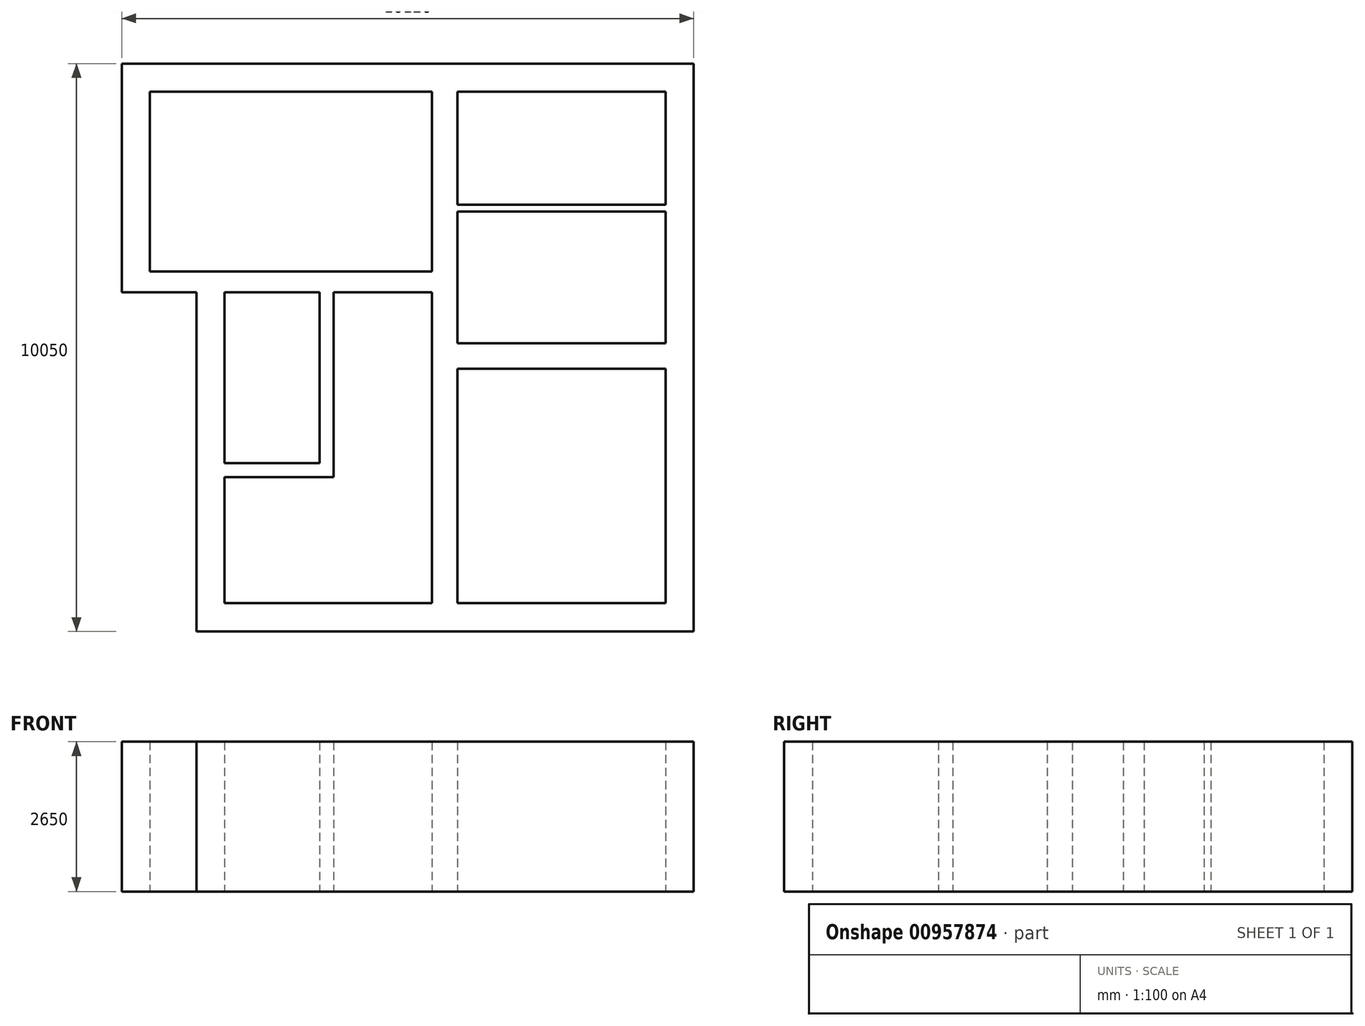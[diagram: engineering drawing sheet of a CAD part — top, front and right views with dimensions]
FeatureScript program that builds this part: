
annotation { "Feature Type Name" : "Feature", "Feature Type Description" : "" }
export const myFeature = defineFeature(function(context is Context, id is Id, definition is map)
    precondition{}
    {
        {
            var Q0;
            Q0=qCreatedBy(makeId("Top.planeOp"),FACE);
            var sketch = newSketch(context, id + "F0", { "sketchPlane" : qUnion([Q0])});
            skLineSegment(sketch, "E0", {"start": v(-6317.16, -9488.66) * mm, "end": v(2482.84, -9488.66) * mm});
            skLineSegment(sketch, "E1", {"start": v(-6317.16, -9488.66) * mm, "end": v(-6317.16, -3488.66) * mm});
            skLineSegment(sketch, "E2", {"start": v(2482.84, -9488.66) * mm, "end": v(2482.84, 561.34) * mm});
            skLineSegment(sketch, "E3", {"start": v(-5817.16, -8988.66) * mm, "end": v(-2147.16, -8988.66) * mm});
            skLineSegment(sketch, "E4", {"start": v(-5817.16, -8988.66) * mm, "end": v(-5817.16, -6758.66) * mm});
            skLineSegment(sketch, "E5", {"start": v(1982.84, 61.34) * mm, "end": v(1982.84, -1938.66) * mm});
            skLineSegment(sketch, "E6", {"start": v(1982.84, 61.34) * mm, "end": v(-1697.16, 61.34) * mm});
            skLineSegment(sketch, "E7", {"start": v(-1697.16, 61.34) * mm, "end": v(-1697.16, -1938.66) * mm});
            skLineSegment(sketch, "E8", {"start": v(-2147.16, 61.34) * mm, "end": v(-2147.16, -8988.66) * mm});
            skLineSegment(sketch, "E9", {"start": v(-2147.16, 61.34) * mm, "end": v(-7137.16, 61.34) * mm});
            skLineSegment(sketch, "E10", {"start": v(-7137.16, 61.34) * mm, "end": v(-7137.16, -3118.66) * mm});
            skLineSegment(sketch, "E11", {"start": v(2482.84, 561.34) * mm, "end": v(-7637.16, 561.34) * mm});
            skLineSegment(sketch, "E12.trimOffspring", {"start": v(-1697.16, -8988.66) * mm, "end": v(1982.84, -8988.66) * mm});
            skLineSegment(sketch, "E13", {"start": v(-7637.16, 561.34) * mm, "end": v(-7637.16, -3488.66) * mm});
            skLineSegment(sketch, "E14", {"start": v(-7637.16, -3488.66) * mm, "end": v(-6317.16, -3488.66) * mm});
            skPoint(sketch, "E15.end.orphan", {"position": v(-7637.16, 61.34) * mm});
            skLineSegment(sketch, "E16", {"start": v(1982.84, -4838.66) * mm, "end": v(-1697.16, -4838.66) * mm});
            skLineSegment(sketch, "E17", {"start": v(-1697.16, -4388.66) * mm, "end": v(1982.84, -4388.66) * mm});
            skLineSegment(sketch, "E18", {"start": v(-5817.16, -3488.66) * mm, "end": v(-4137.16, -3488.66) * mm});
            skLineSegment(sketch, "E19", {"start": v(-4137.16, -3488.66) * mm, "end": v(-4137.16, -6508.66) * mm});
            skLineSegment(sketch, "E20", {"start": v(-3887.16, -6758.66) * mm, "end": v(-3887.16, -3488.66) * mm});
            skLineSegment(sketch, "E21", {"start": v(-3887.16, -6758.66) * mm, "end": v(-5817.16, -6758.66) * mm});
            skLineSegment(sketch, "E22", {"start": v(-4137.16, -6508.66) * mm, "end": v(-5817.16, -6508.66) * mm});
            skLineSegment(sketch, "E23.trimOffspring", {"start": v(-5817.16, -6508.66) * mm, "end": v(-5817.16, -3488.66) * mm});
            skPoint(sketch, "E24.end.orphan", {"position": v(-3887.16, -4463.66) * mm});
            skPoint(sketch, "E24.start.orphan", {"position": v(-2147.16, -4463.66) * mm});
            skLineSegment(sketch, "E25", {"start": v(-7137.16, -3118.66) * mm, "end": v(-2147.16, -3118.66) * mm});
            skLineSegment(sketch, "E26", {"start": v(-3887.16, -3488.66) * mm, "end": v(-2147.16, -3488.66) * mm});
            skLineSegment(sketch, "E27.trimOffspring", {"start": v(-1697.16, -4838.66) * mm, "end": v(-1697.16, -8988.66) * mm});
            skLineSegment(sketch, "E28.trimOffspring", {"start": v(1982.84, -4838.66) * mm, "end": v(1982.84, -8988.66) * mm});
            skLineSegment(sketch, "E29", {"start": v(-1697.16, -2058.66) * mm, "end": v(1982.84, -2058.66) * mm});
            skLineSegment(sketch, "E30", {"start": v(-1697.16, -1938.66) * mm, "end": v(1982.84, -1938.66) * mm});
            skLineSegment(sketch, "E31.trimOffspring", {"start": v(-1697.16, -2058.66) * mm, "end": v(-1697.16, -4388.66) * mm});
            skLineSegment(sketch, "E32.trimOffspring", {"start": v(1982.84, -2058.66) * mm, "end": v(1982.84, -4388.66) * mm});
            skSolve(sketch);
        }
        {
            var Q0;
            Q0 = qSketchRegion(id + "F0", true);
            extrude(context, id + "F1", {"entities" : qUnion([Q0]), "depth" : 2650 * mm, "offsetDistance" : 25 * mm});
        }
    });
